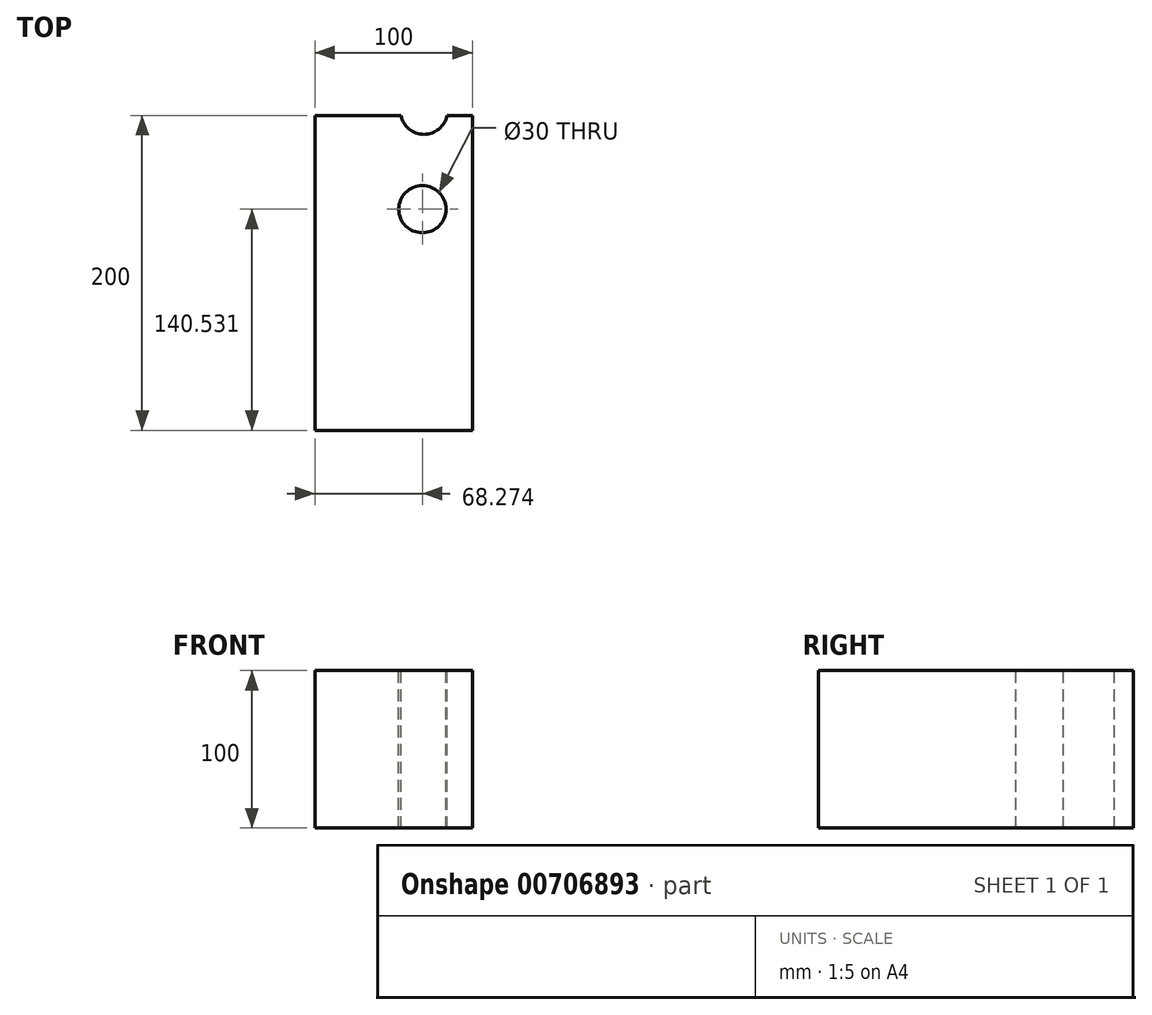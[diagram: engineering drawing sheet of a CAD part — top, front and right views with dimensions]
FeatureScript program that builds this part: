
annotation { "Feature Type Name" : "Feature", "Feature Type Description" : "" }
export const myFeature = defineFeature(function(context is Context, id is Id, definition is map)
    precondition{}
    {
        {
            var Q0;
            Q0=qCreatedBy(makeId("Top.planeOp"),FACE);
            var sketch = newSketch(context, id + "F0", { "sketchPlane" : qUnion([Q0])});
            skLineSegment(sketch, "E0.bottom", {"start": v(50, 100) * mm, "end": v(-50, 100) * mm});
            skLineSegment(sketch, "E0.top", {"start": v(50, -100) * mm, "end": v(-50, -100) * mm});
            skLineSegment(sketch, "E0.left", {"start": v(50, 100) * mm, "end": v(50, -100) * mm});
            skLineSegment(sketch, "E0.right", {"start": v(-50, 100) * mm, "end": v(-50, -100) * mm});
            skSolve(sketch);
        }
        {
            var Q0;
            Q0=makeQuery(id+"F0.imprint","IMPRINT",FACE,{"disambiguationData":[TD([[makeQuery(id+"F0.imprint","IMPRINT",EDGE,{"derivedFrom":sQuery(id+"F0.wireOp",EDGE,"E0.bottom")}),1.0]])]});
            extrude(context, id + "F1", {"entities" : qUnion([Q0]), "depth" : 100 * mm, "offsetDistance" : 25 * mm});
        }
        {
            var Q0;
            Q0=makeQuery(id+"F1.opExtrude","CAP_FACE",FACE,{"disambiguationData":[OSD([sQuery(id+"F0.wireOp",EDGE,"E0.bottom"),sQuery(id+"F0.wireOp",EDGE,"E0.top"),sQuery(id+"F0.wireOp",EDGE,"E0.left"),sQuery(id+"F0.wireOp",EDGE,"E0.right")])],"isStart":false});
            var sketch = newSketch(context, id + "F2", { "sketchPlane" : qUnion([Q0])});
            skCircle(sketch, "E1", {"center": v(18.27, 40.53) * mm, "radius": 15 * mm});
            skCircle(sketch, "E2", {"center": v(12.1, 106.41) * mm, "radius": 15.83 * mm});
            skSolve(sketch);
        }
        {
            var Q0;
            Q0=makeQuery(id+"F2.imprint","IMPRINT",FACE,{"disambiguationData":[TD([[makeQuery(id+"F2.imprint","IMPRINT",EDGE,{"derivedFrom":sQuery(id+"F2.wireOp",EDGE,"E1")}),1.0]])]});
            extrude(context, id + "F3", {"entities" : qUnion([Q0]), "operationType" : NewBodyOperationType.REMOVE, "oppositeDirection" : true, "depth" : 100 * mm, "offsetDistance" : 25 * mm});
        }
        {
            var Q0;
            Q0=makeQuery(id+"F1.opExtrude","CAP_FACE",FACE,{"disambiguationData":[OSD([sQuery(id+"F0.wireOp",EDGE,"E0.bottom"),sQuery(id+"F0.wireOp",EDGE,"E0.top"),sQuery(id+"F0.wireOp",EDGE,"E0.left"),sQuery(id+"F0.wireOp",EDGE,"E0.right")])],"isStart":false});
            var sketch = newSketch(context, id + "F4", { "sketchPlane" : qUnion([Q0])});
            skCircle(sketch, "E3", {"center": v(19.27, 103.03) * mm, "radius": 15 * mm});
            skSolve(sketch);
        }
        {
            var Q0;
            Q0=makeQuery(id+"F4.imprint","IMPRINT",FACE,{"disambiguationData":[TD([[makeQuery(id+"F4.imprint","IMPRINT",EDGE,{"derivedFrom":sQuery(id+"F4.wireOp",EDGE,"E3")}),1.0]])]});
            extrude(context, id + "F5", {"entities" : qUnion([Q0]), "operationType" : NewBodyOperationType.REMOVE, "oppositeDirection" : true, "depth" : 100 * mm, "offsetDistance" : 25 * mm});
        }
    });
